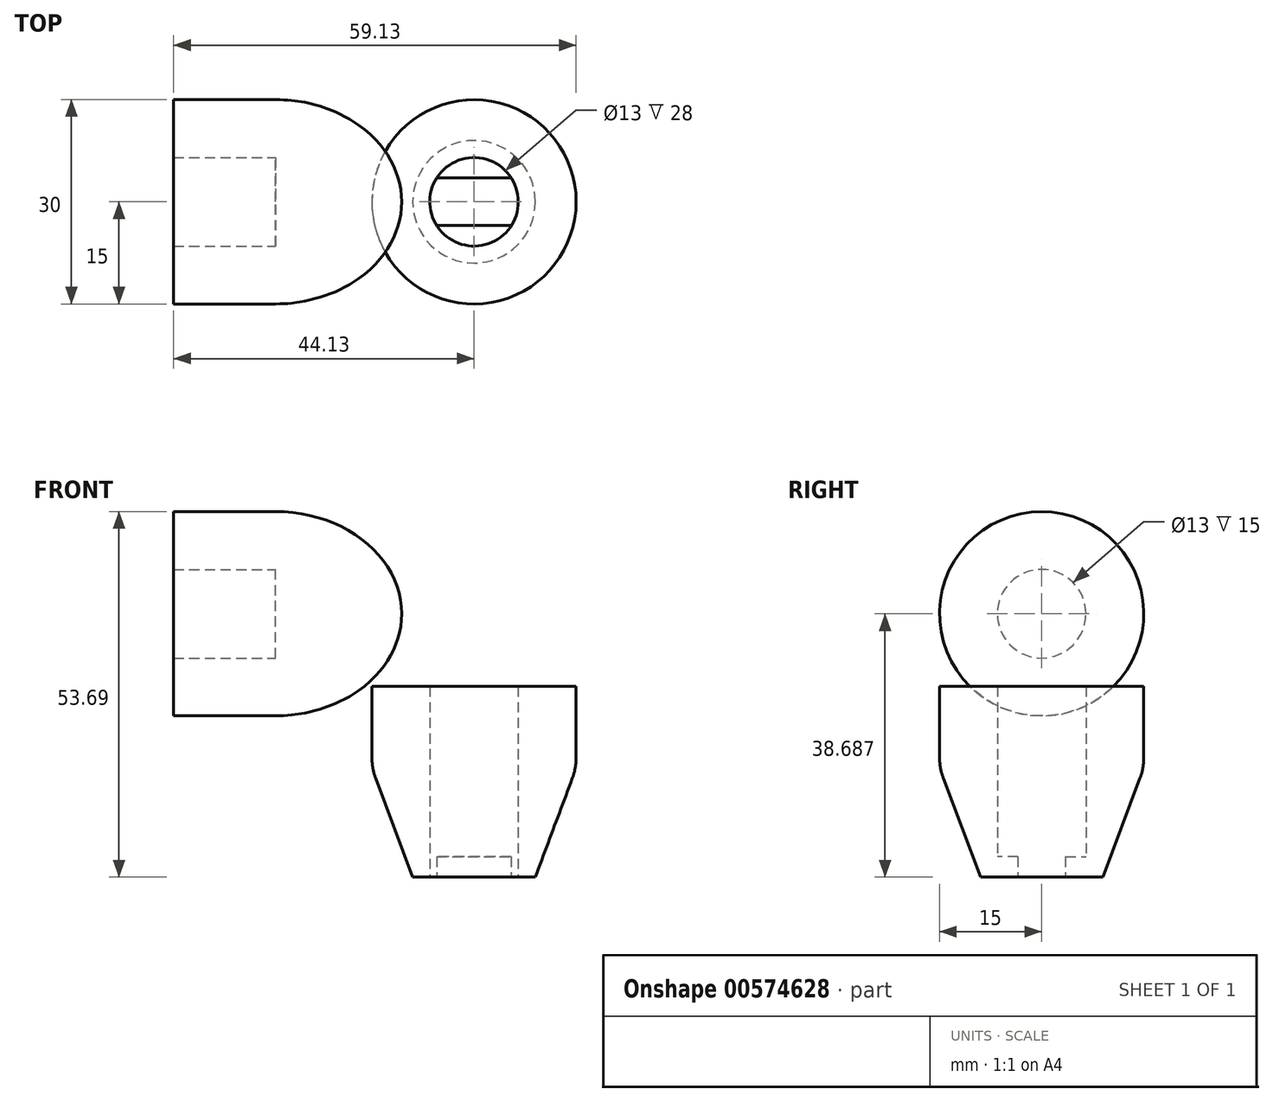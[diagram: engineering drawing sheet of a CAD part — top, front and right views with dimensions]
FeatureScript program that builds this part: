
annotation { "Feature Type Name" : "Feature", "Feature Type Description" : "" }
export const myFeature = defineFeature(function(context is Context, id is Id, definition is map)
    precondition{}
    {
        {
            var Q0;
            Q0=qCreatedBy(makeId("Top.planeOp"),FACE);
            var sketch = newSketch(context, id + "F0", { "sketchPlane" : qUnion([Q0])});
            skCircle(sketch, "E0", {"center": v(0, 0) * mm, "radius": 15 * mm});
            skCircle(sketch, "E1", {"center": v(0, 0) * mm, "radius": 6.5 * mm});
            skPoint(sketch, "E2", {"position": v(0, 3.5) * mm});
            skPoint(sketch, "E3", {"position": v(0, -3.5) * mm});
            skLineSegment(sketch, "E4", {"start": v(-5.48, 3.5) * mm, "end": v(5.48, 3.5) * mm});
            skLineSegment(sketch, "E5", {"start": v(5.48, -3.5) * mm, "end": v(-5.48, -3.5) * mm});
            skSolve(sketch);
        }
        {
            var Q0;
            Q0=makeQuery(id+"F0.imprint","IMPRINT",FACE,{"disambiguationData":[TD([[makeQuery(id+"F0.imprint","IMPRINT",EDGE,{"derivedFrom":sQuery(id+"F0.wireOp",EDGE,"E0")}),1.0]])]});
            extrude(context, id + "F1", {"entities" : qUnion([Q0]), "depth" : 28 * mm, "offsetDistance" : 25 * mm});
        }
        {
            var Q0;
            Q0=makeQuery(id+"F1.opExtrude","CAP_EDGE",EDGE,{"disambiguationData":[OSD([sQuery(id+"F0.wireOp",EDGE,"E0")])],"isStart":true});
            chamfer(context, id + "F2", {"entities" : qUnion([Q0]), "chamferType" : ChamferType.TWO_OFFSETS, "width1" : 16 * mm, "oppositeDirection" : false, "width2" : 6 * mm, "tangentPropagation" : true});
        }
        {
            var Q0;
            {var subQ0=sQuery(id+"F0.wireOp",EDGE,"E0");Q0=makeQuery(id+"F2.opChamfer","BLEND_EDGE",EDGE,{"blendedFrom":[makeQuery(id+"F1.opExtrude","CAP_EDGE",EDGE,{"disambiguationData":[OSD([subQ0])],"isStart":true}),makeQuery(id+"F1.opExtrude","SWEPT_FACE",FACE,{"disambiguationData":[OSD([subQ0])]})],"blendedInto":[makeQuery(id+"F1.opExtrude","SWEPT_FACE",FACE,{"disambiguationData":[OSD([subQ0])]})]});}
            fillet(context, id + "F3", {"entities" : qUnion([Q0]), "radius" : 9 * mm, "tangentPropagation" : true, "allowEdgeOverflow" : false});
        }
        {
            var Q0;
            Q0=qCreatedBy(makeId("Front.planeOp"),FACE);
            var sketch = newSketch(context, id + "F4", { "sketchPlane" : qUnion([Q0])});
            skLineSegment(sketch, "E6.bottom", {"start": v(-44.13, 53.69) * mm, "end": v(-29.13, 53.69) * mm});
            skLineSegment(sketch, "E6.top", {"start": v(-44.13, 38.69) * mm, "end": v(-29.13, 38.69) * mm});
            skLineSegment(sketch, "E6.left", {"start": v(-44.13, 53.69) * mm, "end": v(-44.13, 38.69) * mm});
            skLineSegment(sketch, "E6.right", {"start": v(-29.13, 53.69) * mm, "end": v(-29.13, 38.69) * mm});
            skEllipticalArc(sketch, "E7", {});
            skLineSegment(sketch, "E8", {"start": v(-29.13, 38.69) * mm, "end": v(-10.63, 38.69) * mm});
            skPoint(sketch, "E9", {"position": v(-44.13, 45.19) * mm});
            skLineSegment(sketch, "E10", {"start": v(-44.13, 45.19) * mm, "end": v(-29.13, 45.19) * mm});
            skFitSpline(sketch, "E11.0", {"points": [v(-19.2, 37.8) * mm, v(-19.1, 38.69) * mm, v(-19.2, 39.58) * mm, v(-19.5, 40.38) * mm, v(-19.9, 41.08) * mm, v(-20.43, 41.8) * mm, v(-21.33, 42.7) * mm, v(-22.59, 43.55) * mm, v(-23.78, 44.13) * mm, v(-25.07, 44.62) * mm, v(-26.5, 44.98) * mm, v(-27.99, 45.16) * mm, v(-29.13, 45.2) * mm, v(-30.27, 45.16) * mm, v(-31.77, 44.98) * mm, v(-33.19, 44.62) * mm, v(-34.48, 44.13) * mm, v(-35.68, 43.55) * mm, v(-36.93, 42.7) * mm, v(-37.84, 41.8) * mm, v(-38.37, 41.08) * mm, v(-38.77, 40.38) * mm, v(-39.06, 39.58) * mm, v(-39.17, 38.69) * mm, v(-39.06, 37.8) * mm, v(-38.77, 37) * mm, v(-38.37, 36.3) * mm, v(-37.84, 35.58) * mm, v(-36.93, 34.67) * mm, v(-35.68, 33.83) * mm, v(-34.48, 33.25) * mm, v(-33.19, 32.75) * mm, v(-31.77, 32.4) * mm, v(-30.27, 32.22) * mm, v(-29.13, 32.17) * mm, v(-27.99, 32.22) * mm, v(-26.5, 32.4) * mm, v(-25.07, 32.75) * mm, v(-23.78, 33.25) * mm, v(-22.59, 33.83) * mm, v(-21.33, 34.67) * mm, v(-20.43, 35.58) * mm, v(-19.9, 36.3) * mm, v(-19.5, 37) * mm, v(-19.2, 37.8) * mm, v(-19.1, 38.69) * mm, v(-19.2, 39.58) * mm]});
            skLineSegment(sketch, "E12", {"start": v(0, 38.69) * mm, "end": v(-56.53, 38.69) * mm, "construction": true});
            skPoint(sketch, "E13", {"position": v(-38.13, 38.69) * mm});
            const initialGuessF4  = {"E7": [-0.0291310253739357, 0.03868718209592635, 1, 0, 0.0185, 0.015, 0, 1.5707963267948966]};
            skSetInitialGuess(sketch, initialGuessF4);
            skSolve(sketch);
        }
        {
            var Q0;
            {var subQ0=sQuery(id+"F4.wireOp",EDGE,"E7");Q0=makeQuery(id+"F4.imprint","IMPRINT",FACE,{"disambiguationData":[TD([[makeQuery(id+"F4.imprint","IMPRINT",EDGE,{"derivedFrom":subQ0}),1.0]])]});}
            var Q1;
            {var subQ0=sQuery(id+"F4.wireOp",EDGE,"E6.bottom");Q1=makeQuery(id+"F4.imprint","IMPRINT",FACE,{"disambiguationData":[TD([[makeQuery(id+"F4.imprint","IMPRINT",EDGE,{"derivedFrom":subQ0}),-1.0]])]});}
            var Q2;
            Q2=sQuery(id+"F4.wireOp",EDGE,"E12");
            revolve(context, id + "F5", {"entities" : qUnion([Q0, Q1]), "axis" : qUnion([Q2]), "revolveType" : RevolveType.FULL});
        }
        {
            var Q0;
            {var subQ0=sQuery(id+"F0.wireOp",EDGE,"E4");Q0=makeQuery(id+"F0.imprint","IMPRINT",FACE,{"disambiguationData":[TD([[makeQuery(id+"F0.imprint","IMPRINT",EDGE,{"derivedFrom":subQ0}),1.0]])]});}
            var Q1;
            {var subQ0=sQuery(id+"F0.wireOp",EDGE,"E5");Q1=makeQuery(id+"F0.imprint","IMPRINT",FACE,{"disambiguationData":[TD([[makeQuery(id+"F0.imprint","IMPRINT",EDGE,{"derivedFrom":subQ0}),1.0]])]});}
            extrude(context, id + "F6", {"entities" : qUnion([Q0, Q1]), "operationType" : NewBodyOperationType.ADD, "depth" : 3 * mm, "offsetDistance" : 25 * mm});
        }
    });
